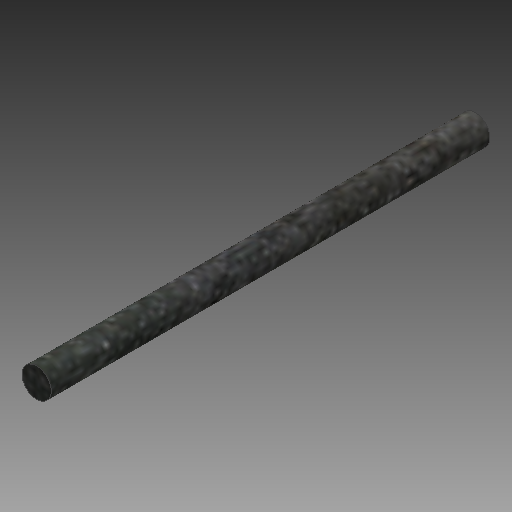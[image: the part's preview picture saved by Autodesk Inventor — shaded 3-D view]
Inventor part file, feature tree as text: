
AUTODESK INVENTOR PART (.ipt)
format: ipt  version: 2018 (Build 220112000, 112)  size: 117,760 bytes
history: native  units: mm
features: other x3, sketch x1
ambient origin geometry x8: Origin, YZ Plane, XZ Plane, XY Plane, X Axis, Y Axis, Z Axis, Center Point
bodies: Volumenkörper1 (feature_tree)
feature tree (4):
  other  "Metall Stab M5.ipt"
  other  "Volumenkörper1::Metall Stab M5.ipt"
  other  "Bezeichnung1"
  sketch  "Skizze1"  dims[d0=10.0mm]
